# Revit family: bs4q14a
name_source: partatom
category: Equipos mecánicos
revit_build: Autodesk Revit 2017 (Build: 20170816_0615(x64)
units: mm (PartAtom-declared; Revit-internal decimal feet)

## family parameters
Anfitrión = Cara
Compartido = No
Corte con vacíos al cargar = No
Cota de conector redondo = Diámetro de uso
Número OmniClass = 23.75.70.17
Punto de cálculo de habitación = Sí
Tipo de pieza = Normal
Título OmniClass = Water Heated and Cooled Terminal Heating and Cooling Units

## types (1)
- bs4q14a
    Casing Material = Galvanised steel plate
    Comentarios de tipo = Accessory
    Código de montaje = 55.10.10.10
    Descripción = Heat Recovery
    Dimensions Unit Height/Width/Depth mm = 298x370x430 mm
    Elevación por defecto = 0 mm  [stored 0 ft]
    Fabricante = Daikin Europe N.V.
    IfcExportAs = IfcUnitaryEquipmentType
    IfcExportType = AIRCONDITIONINGUNIT
    Installation Manual = http://www.daikineurope.com &searchcategory=product-information
    Maximum capacity index of connectable indoor units = 400
    Maximum capacity index of connectable indoor units per branch = 140
    Maximum number of connectable indoor units = 20
    Maximum number of connectable indoor units per branch = 5
    Modelo = VRV BS
    Number of branches = 4
    Piping connections Drain = VP20 (I.D. 20/O.D. 26)
    Piping connections Indoor unit Gas OD mm = 15.9 (1) / 12.7 (2) mm
    Piping connections Indoor unit Liquid OD mm = 9.5 (1) / 6.4 (2) mm
    Piping connections Outdoor unit Discharge gas OD mm = 19.1 / 15.9 (3) mm
    Piping connections Outdoor unit Gas OD mm = 22.2 / 19.1 (3) mm
    Piping connections Outdoor unit Liquid OD mm = 9.5 mm
    Power input Cooling Nom. kW = 0.043 kW
    Power input Heating Nom. kW = 0.043 kW
    Power supply Frequency Hz = 50 Hz
    Power supply Maximum fuse amps (MFA) A = 15 A
    Power supply Phase = 1~
    Power supply Voltage V = 220-440 V
    RSen_C_IFC_version = 2x3
    RSen_C_code_ETIM = Accessories for airconditioning
    RSen_C_code_ETIM_URL = https://prod.etim-international.com
    RSen_C_code_article = BS4Q14AV1
    RSen_C_code_gtin = -
    RSen_C_code_product = BS4Q14A
    RSen_C_code_product_class = BS-Q14A
    RSen_C_content_date_changed = 13/01/2017
    RSen_C_content_date_issue = 13/01/2017
    RSen_C_content_provider = Daikin Europe N.V.
    RSen_C_content_version = v1.0
    RSen_C_description = Heat Recovery
    RSen_C_diameter_type = OD
    RSen_C_diameter_type_index = 1
    RSen_C_height = 298 mm  [stored 0.97769 ft]
    RSen_C_length = 370 mm  [stored 1.21391 ft]
    RSen_C_license = Creative Commons Attribution NoDerivs (CC-ND)
    RSen_C_license_info = https://tldrlegal.com
    RSen_C_material = RSen_x_rgb 255 255 255 T00 pure white_gen
    RSen_C_model = VRV BS
    RSen_C_revit_version = 2015
    RSen_C_type = Multi branch selector for VRV IV Heat Recovery
    RSen_C_type_comments = Accessory
    RSen_C_width = 430 mm
    RSen_E_c01_apparent_power = 92 VA
    RSen_E_c01_current = 0 A
    RSen_E_c01_description = c01_el
    RSen_E_c01_division_engine = No
    RSen_E_c01_load_class = Other
    RSen_E_c01_number_of_poles = 1
    RSen_E_c01_power = 0 W
    RSen_E_c01_power_factor = 1
    RSen_E_c01_power_factor_state = Lagging
    RSen_E_c01_system_type = Power - Balanced
    RSen_E_c01_voltage = 230 V
    RSen_E_c01_yes_no = Sí
    RSen_P_c01_description = c01_outdoor unit suction gas pipe connection
    RSen_P_c01_diameter = 22 mm
    RSen_P_c01_diameter_calc = 22 mm
    RSen_P_c01_flow_configuration = Preset
    RSen_P_c01_flow_direction = Out
    RSen_P_c01_loss_method = Not Defined
    RSen_P_c01_system_classification = Hydronic Return
    RSen_P_c01_yes_no = Sí
    RSen_P_c02_description = c02_outdoor unit HP/LP gas pipe connection
    RSen_P_c02_diameter = 19 mm
    RSen_P_c02_diameter_calc = 19 mm
    RSen_P_c02_flow_configuration = Preset
    RSen_P_c02_flow_direction = Bidirectional
    RSen_P_c02_loss_method = Not Defined
    RSen_P_c02_system_classification = Global
    RSen_P_c02_yes_no = Sí
    RSen_P_c03_description = c03_outdoor unit liquid pipe connection
    RSen_P_c03_diameter = 10 mm  [stored 0.0328084 ft]
    RSen_P_c03_diameter_calc = 10 mm  [stored 0.0328084 ft]
    RSen_P_c03_flow_configuration = Preset
    RSen_P_c03_flow_direction = In
    RSen_P_c03_loss_method = Not Defined
    RSen_P_c03_system_classification = Hydronic Supply
    RSen_P_c03_yes_no = Sí
    RSen_P_c04_description = c04_drain piping connection
    RSen_P_c04_diameter = 26 mm
    RSen_P_c04_diameter_calc = 26 mm
    RSen_P_c04_flow_configuration = Fixture Units
    RSen_P_c04_flow_direction = Out
    RSen_P_c04_loss_method = Not Defined
    RSen_P_c04_system_classification = Sanitary
    RSen_P_c04_yes_no = Sí
    RSen_P_c05_description = c05_Indoor unit liquid pipe connection
    RSen_P_c05_diameter = 10 mm  [stored 0.0328084 ft]
    RSen_P_c05_diameter_calc = 10 mm  [stored 0.0328084 ft]
    RSen_P_c05_flow_configuration = Calculated
    RSen_P_c05_flow_direction = Out
    RSen_P_c05_loss_method = Not Defined
    RSen_P_c05_system_classification = Hydronic Supply
    RSen_P_c05_yes_no = Sí
    RSen_P_c06_description = c06_Indoor unit gas pipe connection
    RSen_P_c06_diameter = 16 mm
    RSen_P_c06_diameter_calc = 16 mm
    RSen_P_c06_flow_configuration = Calculated
    RSen_P_c06_flow_direction = In
    RSen_P_c06_loss_method = Not Defined
    RSen_P_c06_system_classification = Hydronic Return
    RSen_P_c06_yes_no = Sí
    RSen_P_c07_description = c07_Indoor unit liquid pipe connection
    RSen_P_c07_diameter = 10 mm  [stored 0.0328084 ft]
    RSen_P_c07_diameter_calc = 10 mm  [stored 0.0328084 ft]
    RSen_P_c07_yes_no = Sí
    RSen_P_c08_description = c08_Indoor unit gas pipe connection
    RSen_P_c08_diameter = 16 mm
    RSen_P_c08_diameter_calc = 16 mm
    RSen_P_c08_yes_no = Sí
    RSen_P_c09_description = c09_Indoor unit liquid pipe connection
    RSen_P_c09_diameter = 10 mm  [stored 0.0328084 ft]
    RSen_P_c09_diameter_calc = 10 mm  [stored 0.0328084 ft]
    RSen_P_c09_yes_no = Sí
    RSen_P_c10_description = c10_Indoor unit gas pipe connection
    RSen_P_c10_diameter = 16 mm
    RSen_P_c10_diameter_calc = 16 mm
    RSen_P_c10_yes_no = Sí
    RSen_P_c11_description = c11_Indoor unit liquid pipe connection
    RSen_P_c11_diameter = 10 mm  [stored 0.0328084 ft]
    RSen_P_c11_diameter_calc = 10 mm  [stored 0.0328084 ft]
    RSen_P_c11_yes_no = Sí
    RSen_P_c12_description = c12_Indoor unit gas pipe connection
    RSen_P_c12_diameter = 16 mm
    RSen_P_c12_diameter_calc = 16 mm
    RSen_P_c12_yes_no = Sí
    Sound absorbing thermal insulation = Urethane foam, polyethylene foam
    Specification Text = https://my.daikin.eu %3B
    TBQ_I BaseKeynote = 55.10.10.10
    URL = www.daikineurope.com
    Weight Unit kg = 17 kg
    ZZZ_Angled wall mounted_YesNo = No
    ZZZ_Bounding Box_FamilyType_Mechanical Equipment = GEO_bounding box_daikin : standard
    ZZZ_Ceiling mounted_YesNo = No
    ZZZ_Clearance zone_back_Length = 970 mm
    ZZZ_Clearance zone_bottom_Length = 100 mm  [stored 0.328084 ft]
    ZZZ_Clearance zone_front_Length = 500 mm
    ZZZ_Clearance zone_left_Length = 500 mm
    ZZZ_Clearance zone_material_Material = RSen_x_rgb 255 128 128 T80 red_gen
    ZZZ_Clearance zone_right_Length = 300 mm  [stored 0.984252 ft]
    ZZZ_Clearance zone_top_Length = 100 mm  [stored 0.328084 ft]
    ZZZ_Component_01_LOD400_FamilyType_Mechanical Equipment = GEO_none_daikin : standard
    ZZZ_Component_01_X_Length = 0 mm  [stored 0 ft]
    ZZZ_Component_01_Y_Length = 0 mm  [stored 0 ft]
    ZZZ_Component_01_Z_Length = 0 mm  [stored 0 ft]
    ZZZ_Component_01_description_Text = -
    ZZZ_Component_01_height_Length = 298 mm  [stored 0.97769 ft]
    ZZZ_Component_01_length_Length = 370 mm  [stored 1.21391 ft]
    ZZZ_Component_01_material_Material = RSen_x_rgb 255 255 255 T00 pure white_gen
    ZZZ_Component_01_plane_Integer = 1
    ZZZ_Component_01_width_Length = 430 mm
    ZZZ_Component_02_LOD400_FamilyType_Mechanical Equipment = GEO_none_daikin : standard
    ZZZ_Component_02_X_Length = 0 mm  [stored 0 ft]
    ZZZ_Component_02_Y_Length = 0 mm  [stored 0 ft]
    ZZZ_Component_02_Z_Length = 0 mm  [stored 0 ft]
    ZZZ_Component_02_description_Text = -
    ZZZ_Component_02_height_Length = 0 mm  [stored 0 ft]
    ZZZ_Component_02_length_Length = 0 mm  [stored 0 ft]
    ZZZ_Component_02_material_Material = RSen_x_rgb 255 255 255 T00 pure white_gen
    ZZZ_Component_02_plane_Integer = 2
    ZZZ_Component_02_width_Length = 0 mm  [stored 0 ft]
    ZZZ_Component_03_X_Length = 0 mm  [stored 0 ft]
    ZZZ_Component_03_Y_Length = 0 mm  [stored 0 ft]
    ZZZ_Component_03_Z_Length = 0 mm  [stored 0 ft]
    ZZZ_Component_03_description_Text = -
    ZZZ_Component_03_height_Length = 0 mm  [stored 0 ft]
    ZZZ_Component_03_length_Length = 0 mm  [stored 0 ft]
    ZZZ_Component_03_material_Material = RSen_x_rgb 255 255 255 T00 pure white_gen
    ZZZ_Component_03_plane_Integer = 1
    ZZZ_Component_03_width_Length = 0 mm  [stored 0 ft]
    ZZZ_Connection zone_back_Length = 0 mm  [stored 0 ft]
    ZZZ_Connection zone_bottom_Length = 0 mm  [stored 0 ft]
    ZZZ_Connection zone_front_Length = 0 mm  [stored 0 ft]
    ZZZ_Connection zone_left_Length = 0 mm  [stored 0 ft]
    ZZZ_Connection zone_material_Material = RSen_x_rgb 255 128 128 T80 red_gen
    ZZZ_Connection zone_right_Length = 0 mm  [stored 0 ft]
    ZZZ_Connection zone_top_Length = 0 mm  [stored 0 ft]
    ZZZ_Cut out_diameter_Length = 0 mm  [stored 0 ft]
    ZZZ_Cut out_height negative_Length = 2 mm  [stored 0.00656168 ft]
    ZZZ_Cut out_height_Length = 0 mm  [stored 0 ft]
    ZZZ_Cut out_length_Length = 0 mm  [stored 0 ft]
    ZZZ_Cut out_length__Length = 1 mm  [stored 0.00328084 ft]
    ZZZ_Cut out_radius_Length = 1 mm  [stored 0.00328084 ft]
    ZZZ_Cut out_width_Length = 0 mm  [stored 0 ft]
    ZZZ_Cut out_width__Length = 1 mm  [stored 0.00328084 ft]
    ZZZ_E_c01_X_Length = 0 mm  [stored 0 ft]
    ZZZ_E_c01_Y_Length = 0 mm  [stored 0 ft]
    ZZZ_E_c01_Z_Length = 0 mm  [stored 0 ft]
    ZZZ_E_c01_plane_Integer = 2
    ZZZ_Grid_height_Length = 600 mm
    ZZZ_Grid_width_Length = 600 mm
    ZZZ_Half length negative_Length = -185 mm  [stored -0.606955 ft]
    ZZZ_Half width negative_Length = -215 mm
    ZZZ_Height negative_Length = -298 mm  [stored -0.97769 ft]
    ZZZ_Height_Length = 298 mm  [stored 0.97769 ft]
    ZZZ_Length_Length = 370 mm  [stored 1.21391 ft]
    ZZZ_Logo_FamilyType_Generic Models = RSen_55_GM_FB_logo small - SH_daikin : standard
    ZZZ_Logo_Rotation about axis_Angle = 0.00°
    ZZZ_Logo_X_Length = 0 mm  [stored 0 ft]
    ZZZ_Logo_Y_Length = 0 mm  [stored 0 ft]
    ZZZ_Logo_Z_Length = 0 mm  [stored 0 ft]
    ZZZ_Logo_plane_Integer = 2
    ZZZ_Lookup table name_Text = RSen_55_ME_FB_indoor unit - outdoor unit
    ZZZ_Maintenance zone_back_Length = 0 mm  [stored 0 ft]
    ZZZ_Maintenance zone_bottom_Length = 0 mm  [stored 0 ft]
    ZZZ_Maintenance zone_front_Length = 0 mm  [stored 0 ft]
    ZZZ_Maintenance zone_left_Length = 0 mm  [stored 0 ft]
    ZZZ_Maintenance zone_material_Material = RSen_x_rgb 255 128 128 T80 red_gen
    ZZZ_Maintenance zone_right_Length = 0 mm  [stored 0 ft]
    ZZZ_Maintenance zone_top_Length = 0 mm  [stored 0 ft]
    ZZZ_Neighbour unit_offset_back_Length = 0 mm  [stored 0 ft]
    ZZZ_Neighbour unit_offset_front_Length = 0 mm  [stored 0 ft]
    ZZZ_Neighbour unit_offset_left_Length = 0 mm  [stored 0 ft]
    ZZZ_Neighbour unit_offset_right_Length = 0 mm  [stored 0 ft]
    ZZZ_P_c01_X_Length = -92 mm  [stored -0.301837 ft]
    ZZZ_P_c01_Y_Length = 56 mm  [stored 0.183727 ft]
    ZZZ_P_c01_Z_Length = 182 mm  [stored 0.597113 ft]
    ZZZ_P_c01_length_Length = 182 mm  [stored 0.597113 ft]
    ZZZ_P_c01_plane_Integer = 6
    ZZZ_P_c02_X_Length = -136 mm
    ZZZ_P_c02_Y_Length = -61 mm  [stored -0.200131 ft]
    ZZZ_P_c02_Z_Length = 224 mm  [stored 0.734908 ft]
    ZZZ_P_c02_length_Length = 224 mm  [stored 0.734908 ft]
    ZZZ_P_c02_plane_Integer = 6
    ZZZ_P_c03_X_Length = 47 mm  [stored 0.154199 ft]
    ZZZ_P_c03_Y_Length = 63 mm  [stored 0.206693 ft]
    ZZZ_P_c03_Z_Length = 190 mm
    ZZZ_P_c03_length_Length = 190 mm
    ZZZ_P_c03_plane_Integer = 6
    ZZZ_P_c04_X_Length = -35 mm  [stored -0.114829 ft]
    ZZZ_P_c04_Y_Length = 130 mm  [stored 0.426509 ft]
    ZZZ_P_c04_Z_Length = 18 mm  [stored 0.0590551 ft]
    ZZZ_P_c04_length_Length = 18 mm  [stored 0.0590551 ft]
    ZZZ_P_c04_plane_Integer = 6
    ZZZ_P_c05_X_Length = -95 mm
    ZZZ_P_c05_Y_Length = -106 mm  [stored -0.347769 ft]
    ZZZ_P_c05_Z_Length = 159 mm  [stored 0.521654 ft]
    ZZZ_P_c05_length_Length = 159 mm  [stored 0.521654 ft]
    ZZZ_P_c05_plane_Integer = 3
    ZZZ_P_c06_X_Length = -65 mm  [stored -0.213255 ft]
    ZZZ_P_c06_Y_Length = -1 mm  [stored -0.00328084 ft]
    ZZZ_P_c06_Z_Length = 159 mm  [stored 0.521654 ft]
    ZZZ_P_c06_length_Length = 159 mm  [stored 0.521654 ft]
    ZZZ_P_c06_plane_Integer = 3
    ZZZ_P_c07_X_Length = -35 mm  [stored -0.114829 ft]
    ZZZ_P_c07_Y_Length = -106 mm  [stored -0.347769 ft]
    ZZZ_P_c07_Z_Length = 159 mm  [stored 0.521654 ft]
    ZZZ_P_c07_length_Length = 159 mm  [stored 0.521654 ft]
    ZZZ_P_c07_plane_Integer = 3
    ZZZ_P_c08_X_Length = -5 mm  [stored -0.0164042 ft]
    ZZZ_P_c08_Y_Length = -1 mm  [stored -0.00328084 ft]
    ZZZ_P_c08_Z_Length = 159 mm  [stored 0.521654 ft]
    ZZZ_P_c08_length_Length = 159 mm  [stored 0.521654 ft]
    ZZZ_P_c08_plane_Integer = 3
    ZZZ_P_c09_X_Length = 25 mm  [stored 0.082021 ft]
    ZZZ_P_c09_Y_Length = -106 mm  [stored -0.347769 ft]
    ZZZ_P_c09_Z_Length = 159 mm  [stored 0.521654 ft]
    ZZZ_P_c09_length_Length = 159 mm  [stored 0.521654 ft]
    ZZZ_P_c09_plane_Integer = 3
    ZZZ_P_c10_X_Length = 55 mm  [stored 0.180446 ft]
    ZZZ_P_c10_Y_Length = -1 mm  [stored -0.00328084 ft]
    ZZZ_P_c10_Z_Length = 159 mm  [stored 0.521654 ft]
    ZZZ_P_c10_length_Length = 159 mm  [stored 0.521654 ft]
    ZZZ_P_c10_plane_Integer = 3
    ZZZ_P_c11_X_Length = 85 mm  [stored 0.278871 ft]
    ZZZ_P_c11_Y_Length = -106 mm  [stored -0.347769 ft]
    ZZZ_P_c11_Z_Length = 159 mm  [stored 0.521654 ft]
    ZZZ_P_c11_length_Length = 159 mm  [stored 0.521654 ft]
    ZZZ_P_c11_plane_Integer = 3
    ZZZ_P_c12_X_Length = 115 mm  [stored 0.377297 ft]
    ZZZ_P_c12_Y_Length = -1 mm  [stored -0.00328084 ft]
    ZZZ_P_c12_Z_Length = 159 mm  [stored 0.521654 ft]
    ZZZ_P_c12_length_Length = 159 mm  [stored 0.521654 ft]
    ZZZ_P_c12_plane_Integer = 3
    ZZZ_Parallel wall mounted_YesNo = No
    ZZZ_Pendant - horizontal mounted_YesNo = Sí
    ZZZ_Pendant - vertical mounted_YesNo = No
    ZZZ_Placement zone_material_Material = RSen_x_rgb 255 128 128 T80 red_gen
    ZZZ_Recess depth_Length = 0 mm  [stored 0 ft]
    ZZZ_Recess depth_negative_Length = 0 mm  [stored 0 ft]
    ZZZ_Recessed_YesNo = Sí
    ZZZ_Surface mounted_YesNo = No
    ZZZ_Suspension_YesNo = Sí
    ZZZ_Suspension_length_Length = 410 mm  [stored 1.34514 ft]
    ZZZ_Suspension_offset_Length = 20 mm  [stored 0.0656168 ft]
    ZZZ_Suspension_type_FamilyType_Mechanical Equipment = GEO_pendant_gen_witas : Pendant - 2x2 suspension cables_gen
    ZZZ_Suspension_width_Length = 308 mm  [stored 1.0105 ft]
    ZZZ_Symbol_ceiling_FamilyType_Detail Items = RSen_55_DI_FB_mechanical equipment - none_gen_witas : none_gen
    ZZZ_Symbol_wall_FamilyType_Detail Items = RSen_55_DI_FB_mechanical equipment - none_gen_witas : none_gen
    ZZZ_Visualized connectors_FamilyType_Generic Models = RSen_55_GM_FB_none_daikin : standard
    ZZZ_Width_Length = 430 mm
    ZZZ_Zones_plane_Integer = 1

note: [stored X ft] marks values corroborated as IEEE doubles in the binary element streams (Revit-internal decimal feet)

## geometry (parser evidence)
native form markers: Sweep x42
no freeform markers — native parametric forms only
